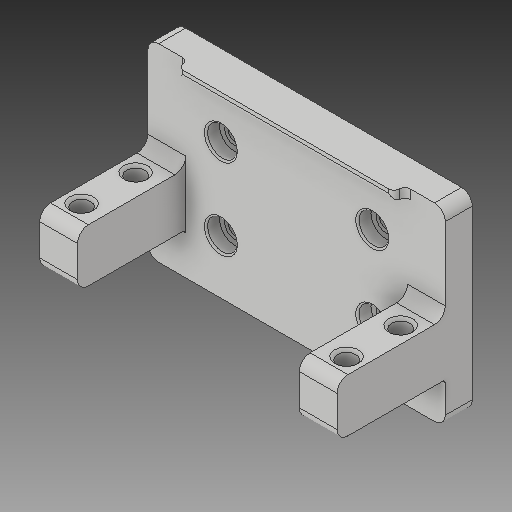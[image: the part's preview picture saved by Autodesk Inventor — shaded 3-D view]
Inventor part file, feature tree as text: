
AUTODESK INVENTOR PART (.ipt)
format: ipt  version: 2019 (Build 230136000, 136)  size: 218,624 bytes
history: native  units: mm
features: sketch x4, other x3
ambient origin geometry x8: Origin, YZ Plane, XZ Plane, XY Plane, X Axis, Y Axis, Z Axis, Center Point
bodies: Solid1 (feature_tree)
feature tree (7):
  other  "big_servo_hold_MIR.ipt"
  other  "Solid1::big_servo_hold_MIR.ipt"
  other  "TaggingFeature1"
  sketch  "Sketch1"  dims[d0=10.0mm]
  sketch  "Sketch2"
  sketch  "Sketch3"
  sketch  "Sketch4"
